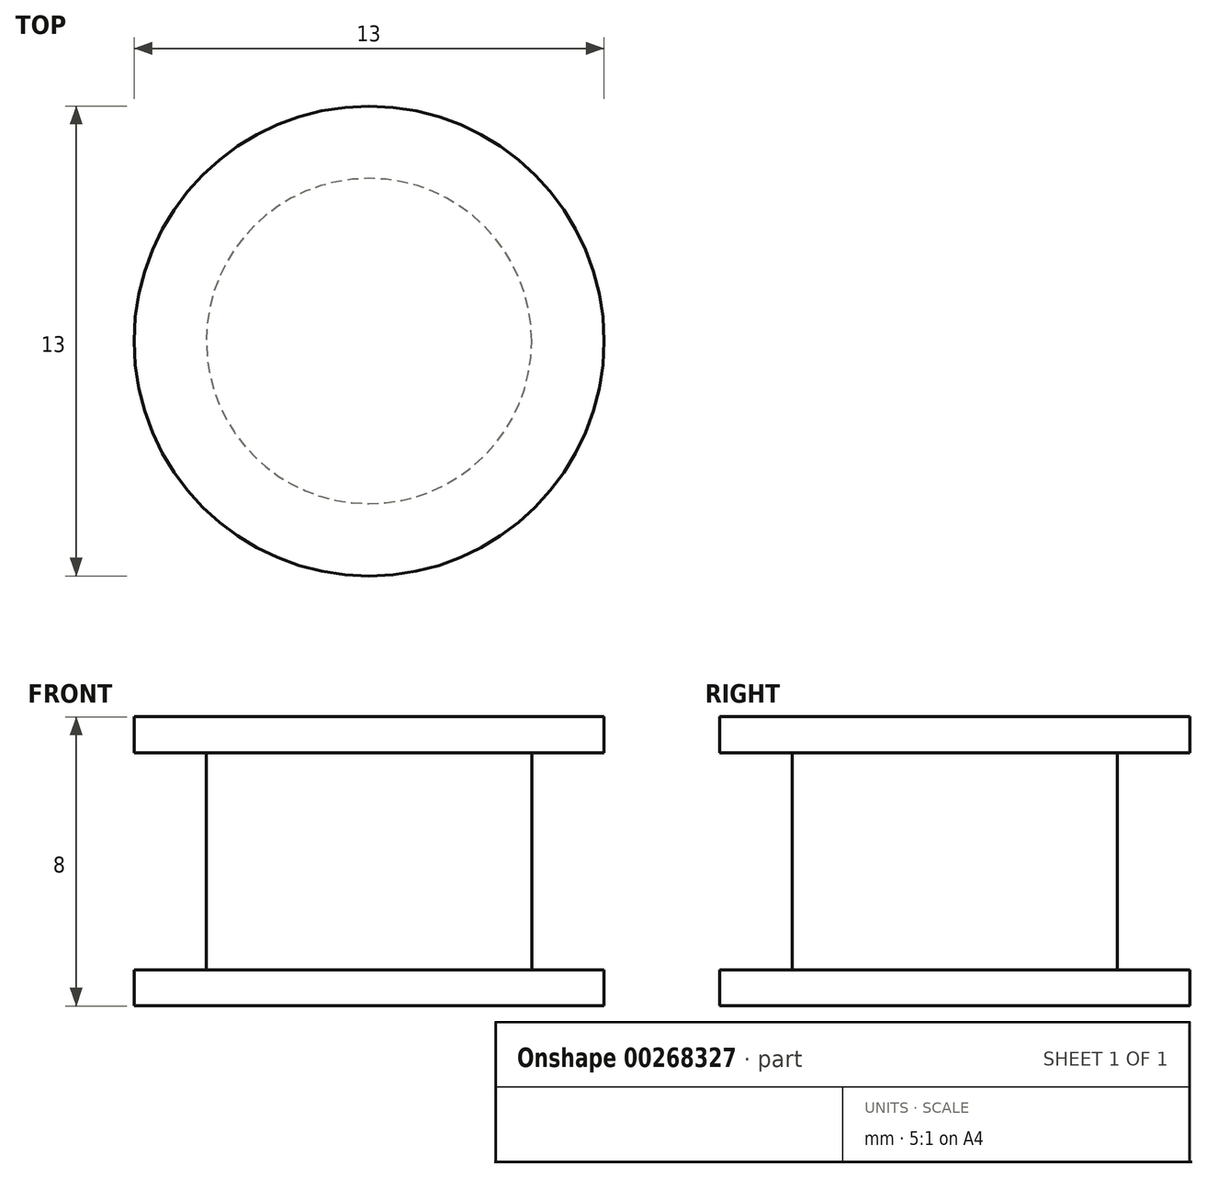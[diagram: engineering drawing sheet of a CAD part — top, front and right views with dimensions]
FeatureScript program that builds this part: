
annotation { "Feature Type Name" : "Feature", "Feature Type Description" : "" }
export const myFeature = defineFeature(function(context is Context, id is Id, definition is map)
    precondition{}
    {
        {
            var Q0;
            Q0=qCreatedBy(makeId("Front.planeOp"),FACE);
            var sketch = newSketch(context, id + "F0", { "sketchPlane" : qUnion([Q0])});
            skLineSegment(sketch, "E0", {"start": v(0, 13.26) * mm, "end": v(6.5, 13.26) * mm});
            skLineSegment(sketch, "E1", {"start": v(6.5, 13.26) * mm, "end": v(6.5, 12.26) * mm});
            skLineSegment(sketch, "E2", {"start": v(6.5, 12.26) * mm, "end": v(4.5, 12.26) * mm});
            skLineSegment(sketch, "E3", {"start": v(4.5, 12.26) * mm, "end": v(4.5, 6.26) * mm});
            skLineSegment(sketch, "E4", {"start": v(4.5, 6.26) * mm, "end": v(6.5, 6.26) * mm});
            skLineSegment(sketch, "E5", {"start": v(6.5, 6.26) * mm, "end": v(6.5, 5.26) * mm});
            skLineSegment(sketch, "E6", {"start": v(6.5, 5.26) * mm, "end": v(0, 5.26) * mm});
            skLineSegment(sketch, "E7", {"start": v(0, 0) * mm, "end": v(0, 3.64) * mm, "construction": true});
            skLineSegment(sketch, "E8", {"start": v(0, 5.26) * mm, "end": v(0, 13.26) * mm});
            skSolve(sketch);
        }
        {
            var Q0;
            Q0=qSketchRegion(id+"F0",true);
            var Q1;
            Q1=sQuery(id+"F0.wireOp",EDGE,"E7");
            revolve(context, id + "F1", {"entities" : qUnion([Q0]), "axis" : qUnion([Q1]), "revolveType" : RevolveType.FULL});
        }
    });
